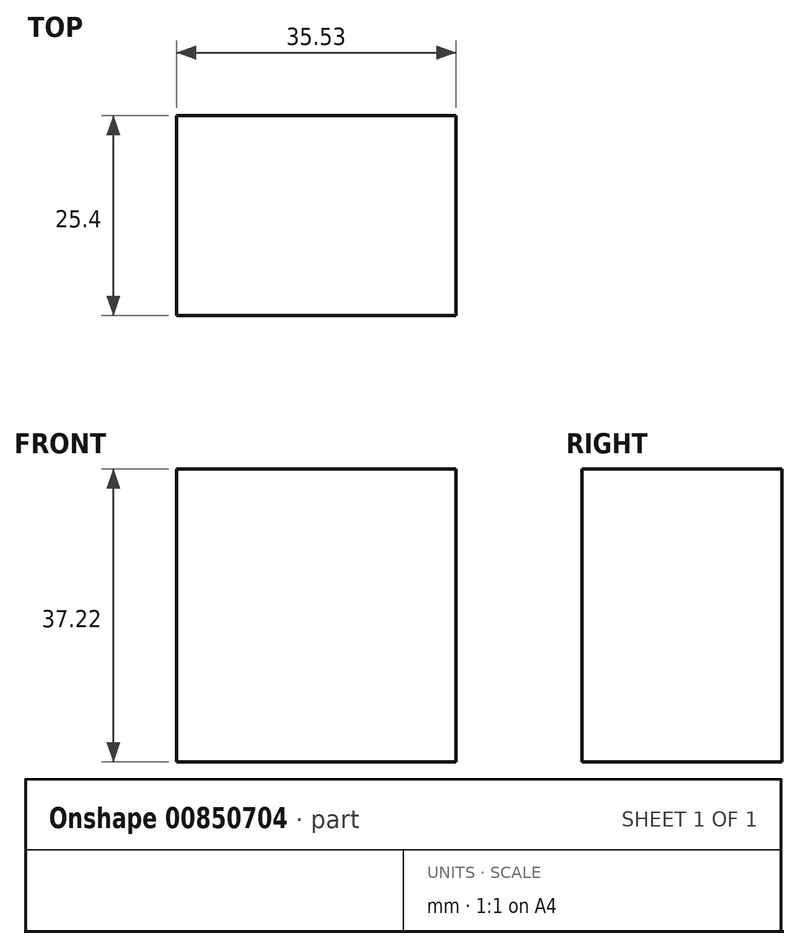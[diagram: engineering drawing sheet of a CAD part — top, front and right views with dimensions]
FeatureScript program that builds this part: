
annotation { "Feature Type Name" : "Feature", "Feature Type Description" : "" }
export const myFeature = defineFeature(function(context is Context, id is Id, definition is map)
    precondition{}
    {
        {
            var Q0;
            Q0=qCreatedBy(makeId("Front.planeOp"),FACE);
            var sketch = newSketch(context, id + "F0", { "sketchPlane" : qUnion([Q0])});
            skLineSegment(sketch, "E0.bottom", {"start": v(-110.66, -18.45) * mm, "end": v(-146.19, -18.45) * mm});
            skLineSegment(sketch, "E0.top", {"start": v(-110.66, 18.77) * mm, "end": v(-146.19, 18.77) * mm});
            skLineSegment(sketch, "E0.left", {"start": v(-110.66, -18.45) * mm, "end": v(-110.66, 18.77) * mm});
            skLineSegment(sketch, "E0.right", {"start": v(-146.19, -18.45) * mm, "end": v(-146.19, 18.77) * mm});
            skSolve(sketch);
        }
        {
            var Q0;
            Q0 = qSketchRegion(id + "F0", true);
            extrude(context, id + "F1", {"entities" : qUnion([Q0]), "depth" : 25.4 * mm, "offsetDistance" : 25.4 * mm});
        }
    });
